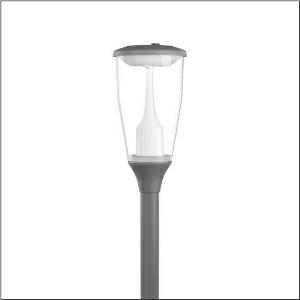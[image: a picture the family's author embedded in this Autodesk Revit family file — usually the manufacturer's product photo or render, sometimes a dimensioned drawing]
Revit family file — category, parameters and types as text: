
# Revit family: dl_11_iq___st1_2a_5xa5575ev14hp00022_13c9
name_source: partatom
category: Lighting Fixtures
units: mm (PartAtom-declared; Revit-internal decimal feet)

## family parameters
Cut with Voids When Loaded = No
Host = Face
Light Source = No
Part Type = Normal
Room Calculation Point = No
Round Connector Dimension = Use Diameter
Shared = No

## types (1)
- --- (1 x LED, 4790 lm, 33.5 W, 3000K)
    Apparent Load = 34 VA
    CIE Flux Codes = 23 60 93 95 100
    Color Rendering = 70
    Color Temperature = 3000K
    Default Elevation = 1800 mm
    Description = DL 11 iQ, mast luminaire, Module 540 iQ-SR, primary light control with 3 zone facetted reflector, of plastic, silver coated, highly specular, structured, primary optical cover: cover, of PMMA, transparent, light distribution: ST1.2a, light emission: direct distribution, primary light characteristic: asymmetric, installation type: post-top, LED, High Power LED, rated luminous flux: 4.790lm, luminous efficacy: 143lm/W, light colour: 730, colour temperature: 3000K, control gear: iQ-Street Remote, D4i with power reduction, control: pre-setting: logarithmic dimming characteristic, Street-Remote, Auto-Match, Temp-Guard, Lumen-Switch, Night-Set, Smart-Wire, Light-Fading, Desk-Remote (wireless, voltage-free reading and setting of iQ features in the workshop via application-optimized NFC function/RFID function), optimised constant luminous flux control (CLO 2.0), mains connection: 220..240V, AC, 50/60Hz, connection cable pre-assembled, cable length: 5,5m, start of lifetime: 34W, end of service life: 36W, reduction: 15W, luminaire housing, upper part, of diecast aluminium, coated, SITECO metallic grey (DB 702S), spigot size: 76mm (post-top), mounting height: 3..5m, post-top mast mounting element, of diecast aluminium, coated, SITECO metallic grey (DB 702S), Module 540 iQ-SR, traffic white (RAL 9016), equipment: Power, Smart Interface above, protection rating (complete): IP66, insulation class (complete): insulation class II (safety insulation), certification: CE, ENEC, ENEC+, VDE, impact resistance: IK07, packaging unit: 1 piece

Light Distribution: ST1.2a
    Height = 665 mm
    Lamp = 1 x LED
    Lamp Light Flux = 4790 lm
    Lamp Power = 33.5 W
    Lamp count = 1
    Length = 334 mm
    Luminous efficacy = 143 lm/W
    Manufacturer = Siteco
    ModVariant = No
    Model = 5XA5575EV14HP00022
    Number of Poles = 1
    OnlyDefault = Yes
    Power Factor = 1
    Product Name = DL 11 iQ | ST1.2a
    Product group = mast luminaire | pylon top
    ProductGroupID = 6100
    Protection Class = Protection class II
    Protection Degree = IP 66
    RLX_Detail_Level = 1
    RLX_Emergency_Light_Flux = 0 lm
    RLX_Emergency_Type = 0
    RLX_Emergency_Type_DB = No
    RlxData = <blob elided: 160341 chars, md5=dd331019>
    Socket = socket
    Standby Power = 0 W
    System Light Flux = 4790 lm
    System Power = 34 W
    Type Comments = factory setting: luminous flux: 100 % | dim-lin: 254 | 695 mA
    Type Image = l_1337541.jpg
    URL = http://relux.com
    VarID = @adj_040463
    Voltage = 0 V
    Weight = 0.00 kg
    Width = 0 mm  [stored 0 ft]

note: [stored X ft] marks values corroborated as IEEE doubles in the binary element streams (Revit-internal decimal feet)

## geometry (parser evidence)
native form markers: Blend x4, Sweep x12
no freeform markers — native parametric forms only
